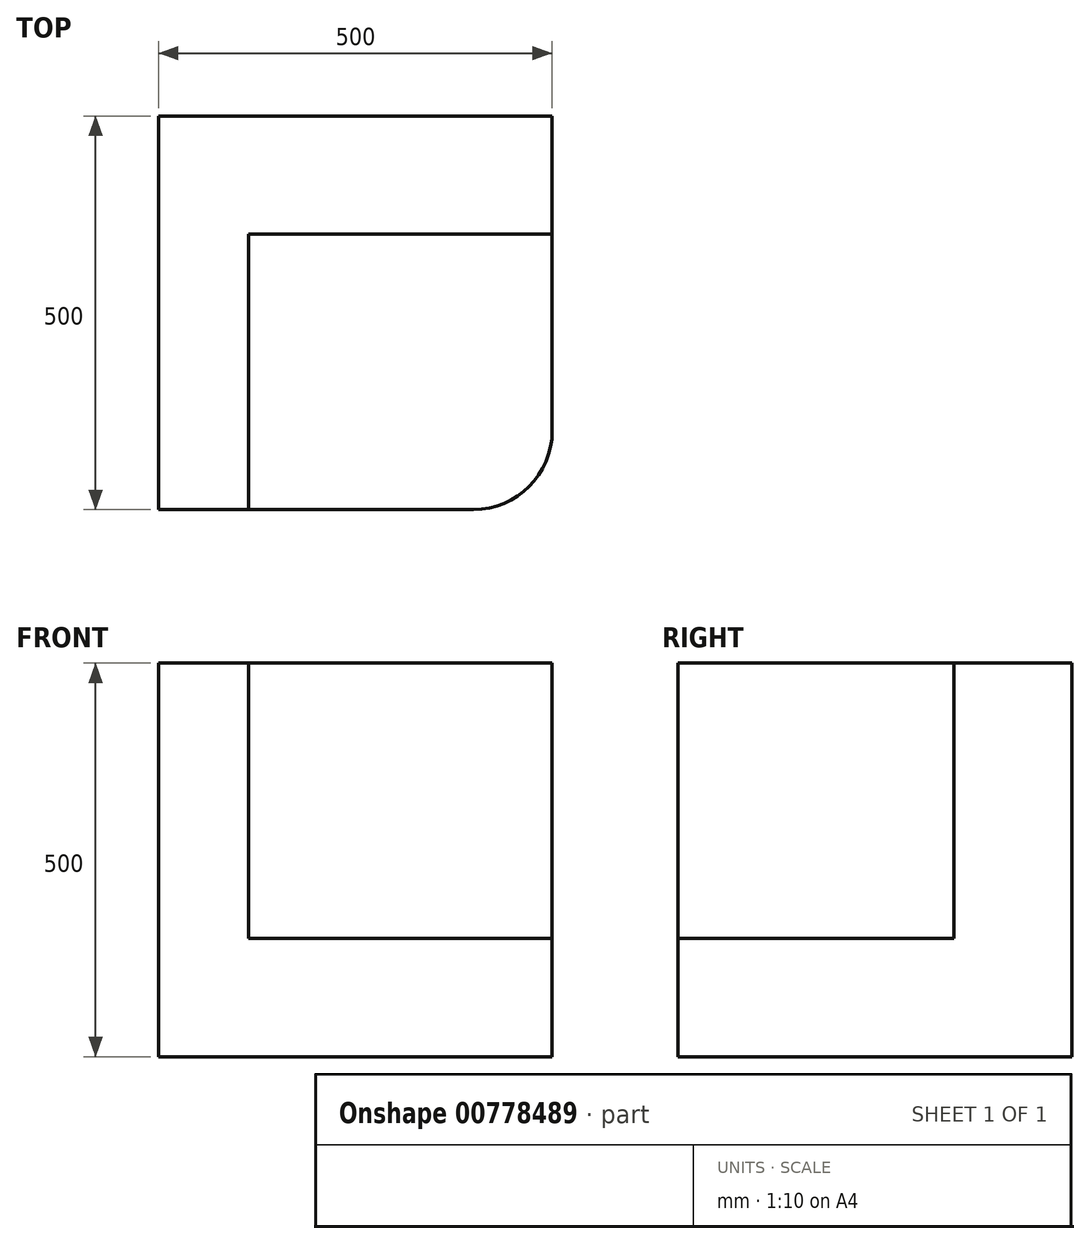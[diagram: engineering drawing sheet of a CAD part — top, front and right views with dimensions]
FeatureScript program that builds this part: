
annotation { "Feature Type Name" : "Feature", "Feature Type Description" : "" }
export const myFeature = defineFeature(function(context is Context, id is Id, definition is map)
    precondition{}
    {
        {
            var Q0;
            Q0=qCreatedBy(makeId("Front.planeOp"),FACE);
            var sketch = newSketch(context, id + "F0", { "sketchPlane" : qUnion([Q0])});
            skLineSegment(sketch, "E0.bottom", {"start": v(0, 0) * mm, "end": v(-500, 0) * mm});
            skLineSegment(sketch, "E0.top", {"start": v(0, 500) * mm, "end": v(-500, 500) * mm});
            skLineSegment(sketch, "E0.left", {"start": v(0, 0) * mm, "end": v(0, 500) * mm});
            skLineSegment(sketch, "E0.right", {"start": v(-500, 0) * mm, "end": v(-500, 500) * mm});
            skSolve(sketch);
        }
        {
            var Q0;
            Q0=makeQuery(id+"F0.imprint","IMPRINT",FACE,{"disambiguationData":[TD([[makeQuery(id+"F0.imprint","IMPRINT",EDGE,{"derivedFrom":sQuery(id+"F0.wireOp",EDGE,"E0.bottom")}),-1.0]])]});
            var sketch = newSketch(context, id + "F1", { "sketchPlane" : qUnion([Q0])});
            skSolve(sketch);
        }
        {
            var Q0;
            Q0=makeQuery(id+"F1.imprint","IMPRINT",FACE,{"disambiguationData":[TD([[makeQuery(id+"F1.imprint","IMPRINT",EDGE,{"derivedFrom":makeQuery(id+"F0.imprint","IMPRINT",EDGE,{"derivedFrom":sQuery(id+"F0.wireOp",EDGE,"E0.bottom")})}),-1.0]])]});
            extrude(context, id + "F2", {"entities" : qUnion([Q0]), "depth" : 500 * mm, "offsetDistance" : 25.4 * mm});
        }
        {
            var Q0;
            Q0=makeQuery(id+"F2.opExtrude","CAP_FACE",FACE,{"disambiguationData":[OSD([sQuery(id+"F0.wireOp",EDGE,"E0.bottom"),sQuery(id+"F0.wireOp",EDGE,"E0.top"),sQuery(id+"F0.wireOp",EDGE,"E0.left"),sQuery(id+"F0.wireOp",EDGE,"E0.right")])],"isStart":false});
            var sketch = newSketch(context, id + "F3", { "sketchPlane" : qUnion([Q0])});
            skLineSegment(sketch, "E1", {"start": v(-500, 500) * mm, "end": v(-385.68, 500) * mm});
            skLineSegment(sketch, "E2", {"start": v(-385.68, 500) * mm, "end": v(-385.68, 150) * mm});
            skLineSegment(sketch, "E3", {"start": v(-385.68, 150) * mm, "end": v(0, 150) * mm});
            skLineSegment(sketch, "E4", {"start": v(0, 150) * mm, "end": v(0, 500) * mm});
            skLineSegment(sketch, "E5", {"start": v(0, 500) * mm, "end": v(-385.68, 500) * mm});
            skSolve(sketch);
        }
        {
            var Q0;
            Q0=makeQuery(id+"F3.imprint","IMPRINT",FACE,{"disambiguationData":[TD([[makeQuery(id+"F3.imprint","IMPRINT",EDGE,{"derivedFrom":sQuery(id+"F3.wireOp",EDGE,"E2")}),1.0]])]});
            extrude(context, id + "F4", {"entities" : qUnion([Q0]), "operationType" : NewBodyOperationType.REMOVE, "oppositeDirection" : true, "depth" : 350 * mm, "offsetDistance" : 25.4 * mm});
        }
        {
            var Q0;
            Q0=makeQuery(id+"F2.opExtrude","CAP_EDGE",EDGE,{"disambiguationData":[OSD([sQuery(id+"F0.wireOp",EDGE,"E0.left")])],"isStart":false});
            fillet(context, id + "F5", {"entities" : qUnion([Q0]), "radius" : 100 * mm, "tangentPropagation" : true, "allowEdgeOverflow" : false});
        }
    });
